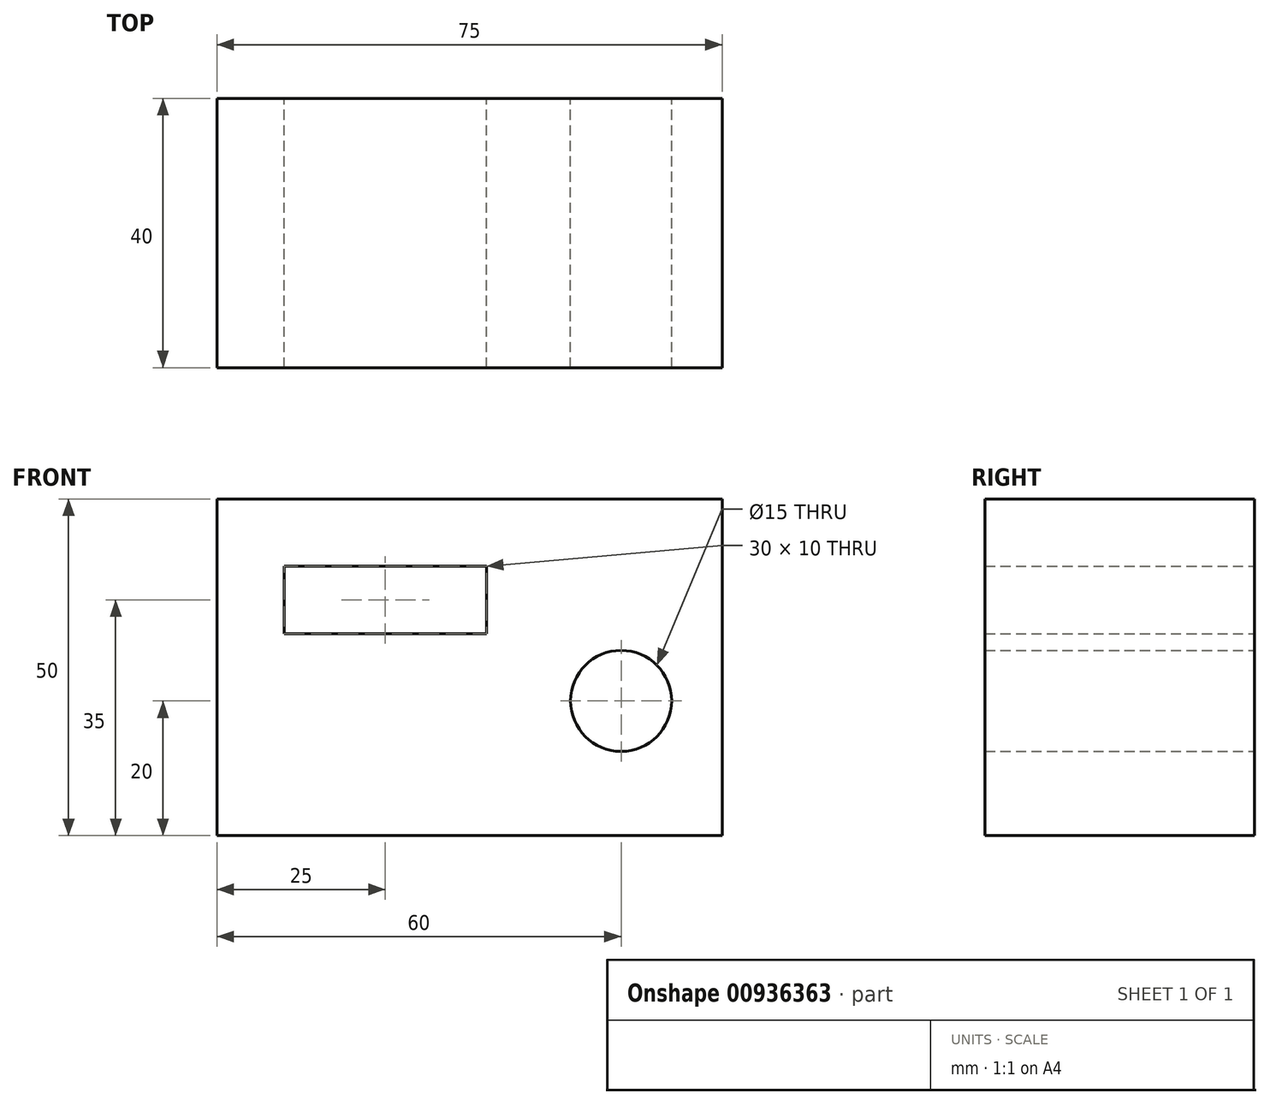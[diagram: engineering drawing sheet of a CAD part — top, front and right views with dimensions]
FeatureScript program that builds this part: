
annotation { "Feature Type Name" : "Feature", "Feature Type Description" : "" }
export const myFeature = defineFeature(function(context is Context, id is Id, definition is map)
    precondition{}
    {
        {
            var Q0;
            Q0=qCreatedBy(makeId("Front.planeOp"),FACE);
            var sketch = newSketch(context, id + "F0", { "sketchPlane" : qUnion([Q0])});
            skLineSegment(sketch, "E0", {"start": v(0, -20) * mm, "end": v(15, -20) * mm});
            skLineSegment(sketch, "E1", {"start": v(15, -20) * mm, "end": v(15, 0) * mm});
            skLineSegment(sketch, "E2", {"start": v(15, 30) * mm, "end": v(15, 0) * mm});
            skLineSegment(sketch, "E3", {"start": v(15, 30) * mm, "end": v(-60, 30) * mm});
            skLineSegment(sketch, "E4", {"start": v(-60, 30) * mm, "end": v(-60, -20) * mm});
            skLineSegment(sketch, "E5", {"start": v(-60, -20) * mm, "end": v(0, -20) * mm});
            skSolve(sketch);
        }
        {
            var Q0;
            Q0=makeQuery(id+"F0.imprint","IMPRINT",FACE,{"disambiguationData":[TD([[makeQuery(id+"F0.imprint","IMPRINT",EDGE,{"derivedFrom":sQuery(id+"F0.wireOp",EDGE,"E0")}),1.0]])]});
            var sketch = newSketch(context, id + "F1", { "sketchPlane" : qUnion([Q0])});
            skCircle(sketch, "E6", {"center": v(0, 0) * mm, "radius": 7.5 * mm});
            skLineSegment(sketch, "E7.bottom", {"start": v(-50, 20) * mm, "end": v(-20, 20) * mm});
            skLineSegment(sketch, "E7.top", {"start": v(-50, 10) * mm, "end": v(-20, 10) * mm});
            skLineSegment(sketch, "E7.left", {"start": v(-50, 20) * mm, "end": v(-50, 10) * mm});
            skLineSegment(sketch, "E7.right", {"start": v(-20, 20) * mm, "end": v(-20, 10) * mm});
            skPoint(sketch, "E7.middle", {"position": v(-35, 15) * mm});
            skSolve(sketch);
        }
        {
            var Q0;
            Q0=makeQuery(id+"F1.imprint","IMPRINT",FACE,{"disambiguationData":[TD([[makeQuery(id+"F1.imprint","IMPRINT",EDGE,{"derivedFrom":sQuery(id+"F1.wireOp",EDGE,"E6")}),-1.0]])]});
            extrude(context, id + "F2", {"entities" : qUnion([Q0]), "depth" : 40 * mm, "offsetDistance" : 25 * mm, "symmetric" : true});
        }
    });
